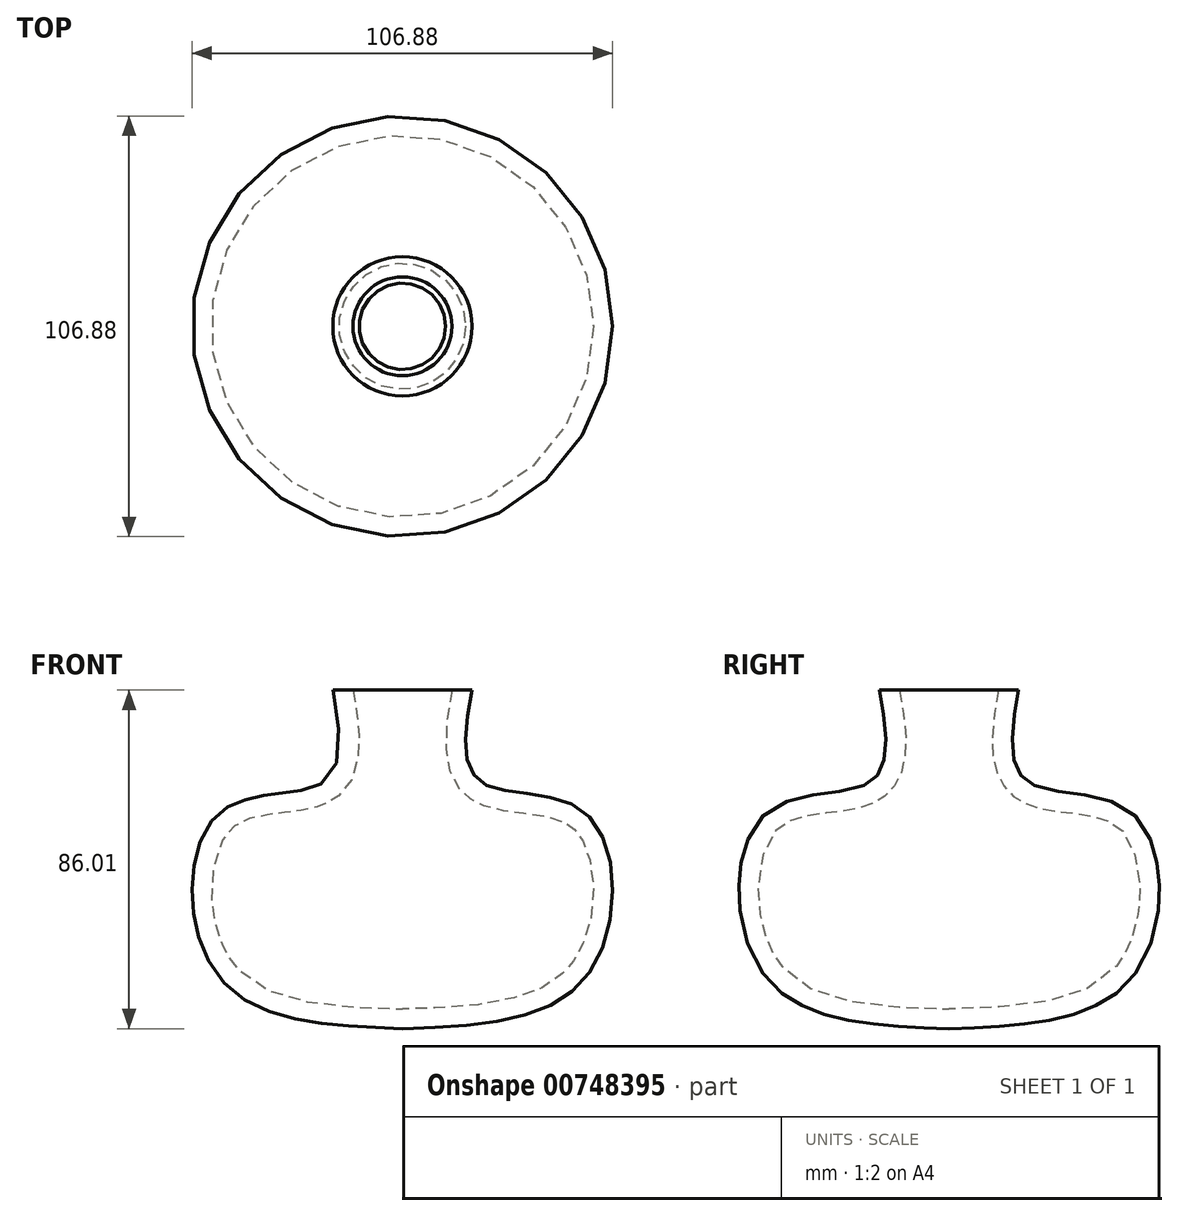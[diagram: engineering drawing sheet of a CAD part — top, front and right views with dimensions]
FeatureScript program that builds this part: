
annotation { "Feature Type Name" : "Feature", "Feature Type Description" : "" }
export const myFeature = defineFeature(function(context is Context, id is Id, definition is map)
    precondition{}
    {
        {
            var Q0;
            Q0=qCreatedBy(makeId("Front.planeOp"),FACE);
            var sketch = newSketch(context, id + "F0", { "sketchPlane" : qUnion([Q0])});
            skFitSpline(sketch, "E0", {"points": [v(18.7, 54.67) * mm, v(19.53, 26.56) * mm, v(46.52, 18.41) * mm, v(47.36, -22.35) * mm, v(0, -36.4) * mm], "startDerivative": vector(-32.79, -160.55) * mm, "endDerivative": vector(-196.24, -7.07) * mm});
            skFitSpline(sketch, "E1.0", {"points": [v(13.8, 55.67) * mm, v(13.45, 54) * mm, v(12.76, 50.62) * mm, v(11.84, 45.56) * mm, v(11.19, 40.6) * mm, v(11, 36.6) * mm, v(11.16, 33.5) * mm, v(11.49, 31.2) * mm, v(12.08, 28.93) * mm, v(13, 26.72) * mm, v(14.11, 24.98) * mm, v(15.22, 23.7) * mm, v(16, 22.98) * mm, v(16.68, 22.44) * mm, v(17.38, 21.95) * mm, v(18.26, 21.41) * mm, v(19.34, 20.88) * mm, v(20.8, 20.28) * mm, v(22.61, 19.73) * mm, v(24.8, 19.25) * mm, v(26.97, 18.9) * mm, v(29.14, 18.6) * mm, v(31.28, 18.34) * mm, v(34.06, 17.98) * mm, v(36.67, 17.52) * mm, v(38.98, 16.89) * mm, v(40.53, 16.32) * mm, v(41.65, 15.76) * mm, v(42.43, 15.26) * mm, v(42.98, 14.86) * mm, v(43.48, 14.43) * mm, v(43.97, 13.94) * mm, v(44.44, 13.39) * mm, v(45.06, 12.56) * mm, v(45.8, 11.37) * mm, v(46.57, 9.7) * mm, v(47.24, 7.8) * mm, v(47.94, 5.05) * mm, v(48.46, 1.24) * mm, v(48.46, -3.64) * mm, v(47.83, -8.55) * mm, v(46.78, -12.42) * mm, v(45.67, -15.27) * mm, v(44.7, -17.24) * mm, v(43.8, -18.72) * mm, v(43.04, -19.8) * mm, v(42.23, -20.81) * mm, v(41.14, -22) * mm, v(39.2, -23.7) * mm, v(36.43, -25.52) * mm, v(32.5, -27.3) * mm, v(27.99, -28.68) * mm, v(21.33, -30.04) * mm, v(11.99, -30.96) * mm, v(3.9, -31.26) * mm, v(-0.18, -31.4) * mm]});
            skLineSegment(sketch, "E2", {"start": v(4.36, 49.6) * mm, "end": v(33.87, 49.6) * mm});
            skLineSegment(sketch, "E3", {"start": v(0, 49.33) * mm, "end": v(0, -36.4) * mm});
            skSolve(sketch);
        }
        {
            var Q0;
            {var subQ0=sQuery(id+"F0.wireOp",EDGE,"E3");var subQ1=sQuery(id+"F0.wireOp",EDGE,"E0");var subQ2=makeQuery(id+"F0.imprint","INTERSECT",VERTEX,{"derivedFrom":[subQ1,subQ0]});Q0=makeQuery(id+"F0.imprint","IMPRINT",FACE,{"disambiguationData":[TD([[makeQuery(id+"F0.imprint","IMPRINT",EDGE,{"disambiguationData":[TD([[subQ2,1.0]])],"derivedFrom":subQ1}),-1.0]])]});}
            var Q1;
            Q1=sQuery(id+"F0.wireOp",EDGE,"E3");
            revolve(context, id + "F1", {"surfaceOperationType" : NewSurfaceOperationType.NEW, "entities" : qUnion([Q0]), "axis" : qUnion([Q1]), "revolveType" : RevolveType.FULL});
        }
    });
